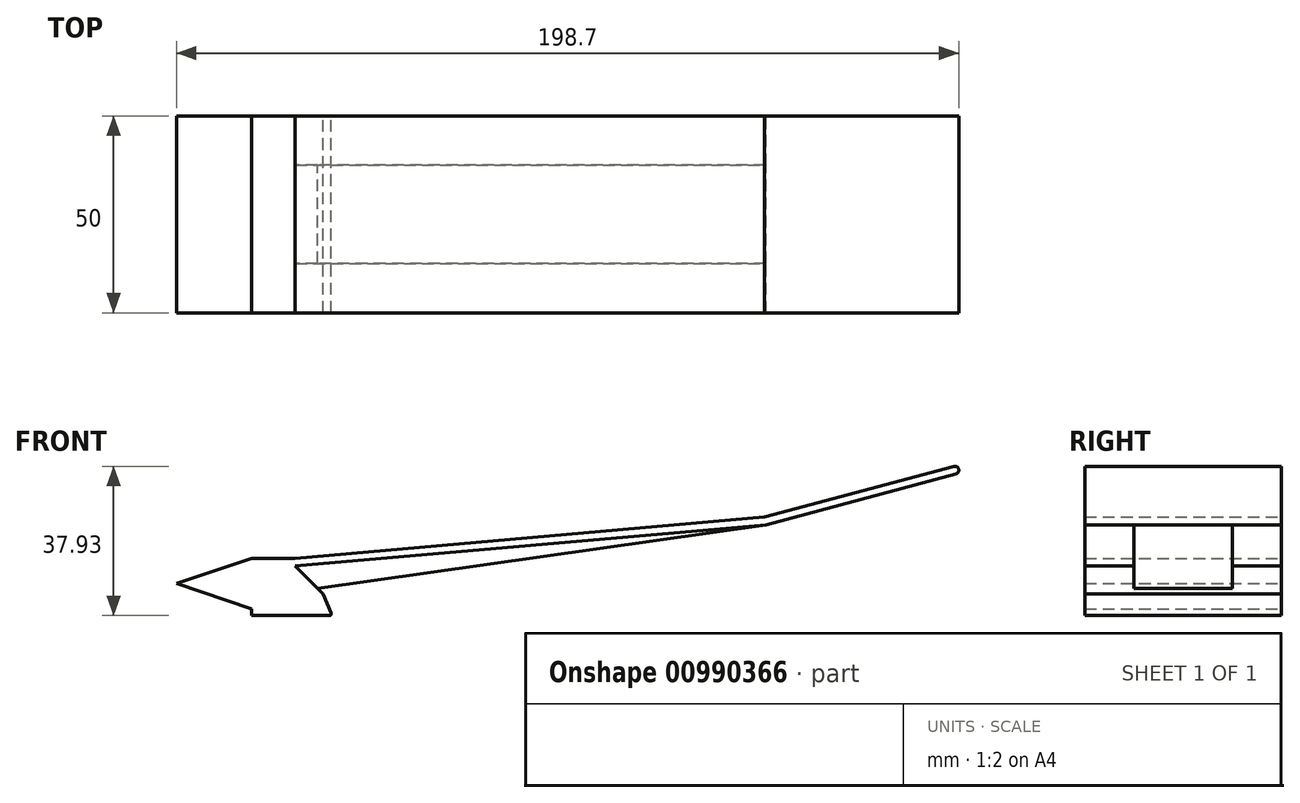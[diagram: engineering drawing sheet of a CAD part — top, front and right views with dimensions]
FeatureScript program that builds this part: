
annotation { "Feature Type Name" : "Feature", "Feature Type Description" : "" }
export const myFeature = defineFeature(function(context is Context, id is Id, definition is map)
    precondition{}
    {
        {
            var Q0;
            Q0=qCreatedBy(makeId("Front.planeOp"),FACE);
            var sketch = newSketch(context, id + "F0", { "sketchPlane" : qUnion([Q0])});
            skLineSegment(sketch, "E0", {"start": v(-4.46, -6.11) * mm, "end": v(-2.4, -10.92) * mm});
            skPoint(sketch, "E1.visualSharp", {"position": v(-2.11, -11.61) * mm});
            skArc(sketch, "E1.filletArc", {"start": v(-2.87, -11.61) * mm, "mid": v(-2.45, -11.39) * mm, "end": v(-2.4, -10.92) * mm});
            skLineSegment(sketch, "E2", {"start": v(-23.57, -9.91) * mm, "end": v(-23.57, -11.61) * mm});
            skLineSegment(sketch, "E3", {"start": v(-4.46, -6.11) * mm, "end": v(-11.53, 0.96) * mm});
            skLineSegment(sketch, "E4", {"start": v(-11.53, 0.96) * mm, "end": v(108.01, 11.42) * mm});
            skLineSegment(sketch, "E5", {"start": v(108.01, 11.42) * mm, "end": v(156.3, 24.36) * mm});
            skLineSegment(sketch, "E6.1", {"start": v(107.66, 13.4) * mm, "end": v(155.79, 26.29) * mm});
            skLineSegment(sketch, "E6.2", {"start": v(-11.62, 2.96) * mm, "end": v(107.66, 13.4) * mm});
            skArc(sketch, "E7", {"start": v(155.79, 26.29) * mm, "mid": v(157.01, 25.58) * mm, "end": v(156.3, 24.36) * mm});
            skLineSegment(sketch, "E8", {"start": v(108.01, 11.42) * mm, "end": v(-5.88, -4.7) * mm});
            skLineSegment(sketch, "E9", {"start": v(-23.57, 2.96) * mm, "end": v(-42.65, -3.48) * mm});
            skLineSegment(sketch, "E10", {"start": v(-42.65, -3.48) * mm, "end": v(-23.57, -9.91) * mm});
            skLineSegment(sketch, "E11", {"start": v(-11.62, 2.96) * mm, "end": v(-22.57, 2.96) * mm});
            skLineSegment(sketch, "E12", {"start": v(-2.87, -11.61) * mm, "end": v(-22.57, -11.61) * mm});
            skLineSegment(sketch, "E13", {"start": v(-22.57, -11.61) * mm, "end": v(-22.57, -9.91) * mm});
            skLineSegment(sketch, "E14", {"start": v(-42.65, -3.48) * mm, "end": v(-41.65, -3.48) * mm});
            skLineSegment(sketch, "E15", {"start": v(-22.57, 2.96) * mm, "end": v(-41.65, -3.48) * mm});
            skLineSegment(sketch, "E16", {"start": v(-22.57, -9.91) * mm, "end": v(-41.65, -3.48) * mm});
            skSolve(sketch);
        }
        {
            var Q0;
            {var subQ1=sQuery(id+"F0.wireOp",EDGE,"E0");Q0=makeQuery(id+"F0.imprint","IMPRINT",FACE,{"disambiguationData":[TD([[makeQuery(id+"F0.imprint","IMPRINT",EDGE,{"derivedFrom":subQ1}),-1.0]])]});}
            extrude(context, id + "F1", {"entities" : qUnion([Q0]), "endBound" : BoundingType.SYMMETRIC, "depth" : 50 * mm, "offsetDistance" : 25 * mm});
        }
        {
            var Q0;
            {var subQ0=sQuery(id+"F0.wireOp",EDGE,"E4");Q0=makeQuery(id+"F0.imprint","IMPRINT",FACE,{"disambiguationData":[TD([[makeQuery(id+"F0.imprint","IMPRINT",EDGE,{"derivedFrom":subQ0}),-1.0]])]});}
            extrude(context, id + "F2", {"entities" : qUnion([Q0]), "operationType" : NewBodyOperationType.ADD, "endBound" : BoundingType.SYMMETRIC, "depth" : 25 * mm, "offsetDistance" : 25 * mm});
        }
    });
